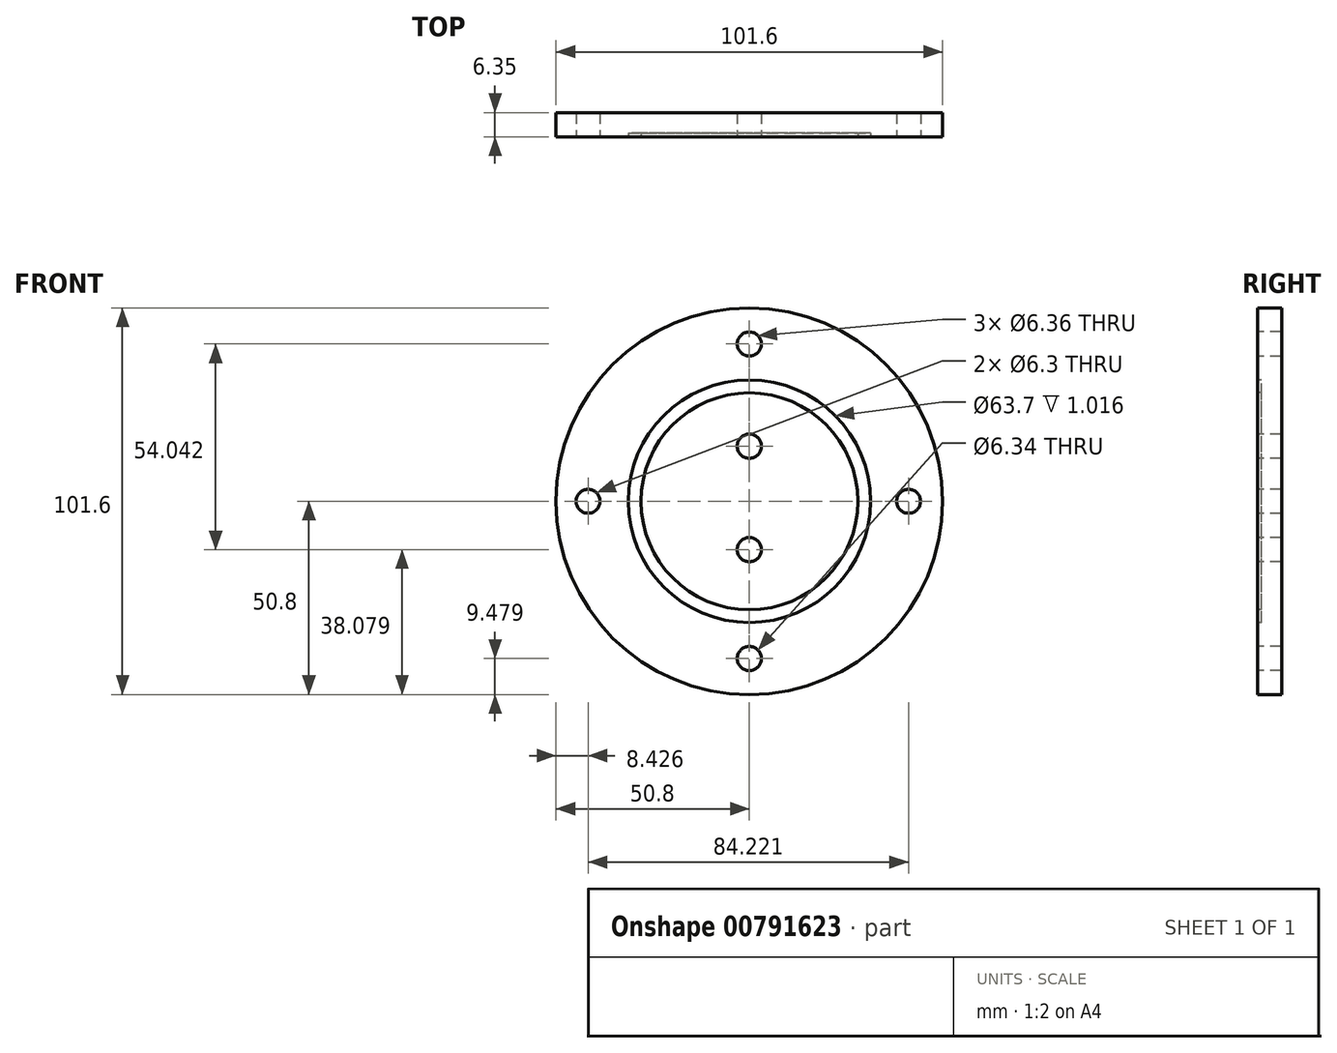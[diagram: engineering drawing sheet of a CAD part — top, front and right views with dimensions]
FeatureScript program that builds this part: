
annotation { "Feature Type Name" : "Feature", "Feature Type Description" : "" }
export const myFeature = defineFeature(function(context is Context, id is Id, definition is map)
    precondition{}
    {
        {
            var Q0;
            Q0=qCreatedBy(makeId("Front.planeOp"),FACE);
            var sketch = newSketch(context, id + "F0", { "sketchPlane" : qUnion([Q0])});
            skCircle(sketch, "E0", {"center": v(0, 0) * mm, "radius": 50.8 * mm});
            skSolve(sketch);
        }
        {
            var Q0;
            Q0 = qSketchRegion(id + "F0", true);
            extrude(context, id + "F1", {"entities" : qUnion([Q0]), "depth" : 6.35 * mm, "offsetDistance" : 25.4 * mm});
        }
        {
            var Q0;
            Q0=makeQuery(id+"F1.opExtrude","CAP_FACE",FACE,{"disambiguationData":[OSD([sQuery(id+"F0.wireOp",EDGE,"E0")])],"isStart":false});
            var sketch = newSketch(context, id + "F2", { "sketchPlane" : qUnion([Q0])});
            skCircle(sketch, "E1", {"center": v(0, 0) * mm, "radius": 28.5 * mm});
            skCircle(sketch, "E2", {"center": v(0, 0) * mm, "radius": 31.85 * mm});
            skSolve(sketch);
        }
        {
            var Q0;
            Q0=makeQuery(id+"F2.imprint","IMPRINT",FACE,{"disambiguationData":[TD([[makeQuery(id+"F2.imprint","IMPRINT",EDGE,{"derivedFrom":sQuery(id+"F2.wireOp",EDGE,"E1")}),-1.0]])]});
            extrude(context, id + "F3", {"entities" : qUnion([Q0]), "operationType" : NewBodyOperationType.REMOVE, "oppositeDirection" : true, "depth" : 1.02 * mm, "offsetDistance" : 25.4 * mm});
        }
        {
            var Q0;
            Q0=makeQuery(id+"F3.boolean.opBoolean","SPLIT",FACE,{"disambiguationData":[TD([makeQuery(id+"F3.opExtrude","SWEPT_FACE",FACE,{"disambiguationData":[OSD([sQuery(id+"F2.wireOp",EDGE,"E1")])]})])],"derivedFrom":makeQuery(id+"F1.opExtrude","CAP_FACE",FACE,{"disambiguationData":[OSD([sQuery(id+"F0.wireOp",EDGE,"E0")])],"isStart":false})});
            var sketch = newSketch(context, id + "F4", { "sketchPlane" : qUnion([Q0])});
            skCircle(sketch, "E3", {"center": v(0, 14.48) * mm, "radius": 3.18 * mm});
            skCircle(sketch, "E4", {"center": v(0, -9.21) * mm, "radius": 3.2 * mm});
            skSolve(sketch);
        }
        {
            var Q0;
            Q0=makeQuery(id+"F4.imprint","IMPRINT",FACE,{"disambiguationData":[TD([[makeQuery(id+"F4.imprint","IMPRINT",EDGE,{"derivedFrom":sQuery(id+"F4.wireOp",EDGE,"E3")}),1.0]])]});
            extrude(context, id + "F5", {"entities" : qUnion([Q0]), "operationType" : NewBodyOperationType.REMOVE, "oppositeDirection" : true, "depth" : 25.4 * mm, "offsetDistance" : 25.4 * mm});
        }
        {
            var Q0;
            Q0=makeQuery(id+"F3.boolean.opBoolean","SPLIT",FACE,{"disambiguationData":[TD([makeQuery(id+"F3.opExtrude","SWEPT_FACE",FACE,{"disambiguationData":[OSD([sQuery(id+"F2.wireOp",EDGE,"E1")])]})])],"derivedFrom":makeQuery(id+"F1.opExtrude","CAP_FACE",FACE,{"disambiguationData":[OSD([sQuery(id+"F0.wireOp",EDGE,"E0")])],"isStart":false})});
            var sketch = newSketch(context, id + "F6", { "sketchPlane" : qUnion([Q0])});
            skCircle(sketch, "E5", {"center": v(0, -12.72) * mm, "radius": 3.18 * mm});
            skSolve(sketch);
        }
        {
            var Q0;
            Q0=makeQuery(id+"F6.imprint","IMPRINT",FACE,{"disambiguationData":[TD([[makeQuery(id+"F6.imprint","IMPRINT",EDGE,{"derivedFrom":sQuery(id+"F6.wireOp",EDGE,"E5")}),1.0]])]});
            extrude(context, id + "F7", {"entities" : qUnion([Q0]), "operationType" : NewBodyOperationType.REMOVE, "oppositeDirection" : true, "depth" : 25.4 * mm, "offsetDistance" : 25.4 * mm});
        }
        {
            var Q0;
            {var subQ0=sQuery(id+"F0.wireOp",EDGE,"E0");Q0=makeQuery(id+"F3.boolean.opBoolean","SPLIT",FACE,{"disambiguationData":[TD([makeQuery(id+"F1.opExtrude","SWEPT_FACE",FACE,{"disambiguationData":[OSD([subQ0])]})])],"derivedFrom":makeQuery(id+"F1.opExtrude","CAP_FACE",FACE,{"disambiguationData":[OSD([subQ0])],"isStart":false})});}
            var sketch = newSketch(context, id + "F8", { "sketchPlane" : qUnion([Q0])});
            skCircle(sketch, "E6", {"center": v(0, 41.32) * mm, "radius": 3.18 * mm});
            skSolve(sketch);
        }
        {
            var Q0;
            Q0 = qSketchRegion(id + "F8", true);
            extrude(context, id + "F9", {"entities" : qUnion([Q0]), "operationType" : NewBodyOperationType.REMOVE, "oppositeDirection" : true, "depth" : 25.4 * mm, "offsetDistance" : 25.4 * mm});
        }
        {
            var Q0;
            {var subQ0=sQuery(id+"F0.wireOp",EDGE,"E0");Q0=makeQuery(id+"F3.boolean.opBoolean","SPLIT",FACE,{"disambiguationData":[TD([makeQuery(id+"F1.opExtrude","SWEPT_FACE",FACE,{"disambiguationData":[OSD([subQ0])]})])],"derivedFrom":makeQuery(id+"F1.opExtrude","CAP_FACE",FACE,{"disambiguationData":[OSD([subQ0])],"isStart":false})});}
            var sketch = newSketch(context, id + "F10", { "sketchPlane" : qUnion([Q0])});
            skCircle(sketch, "E7", {"center": v(41.85, 0) * mm, "radius": 3.15 * mm});
            skSolve(sketch);
        }
        {
            var Q0;
            Q0=makeQuery(id+"F10.imprint","IMPRINT",FACE,{"disambiguationData":[TD([[makeQuery(id+"F10.imprint","IMPRINT",EDGE,{"derivedFrom":sQuery(id+"F10.wireOp",EDGE,"E7")}),1.0]])]});
            extrude(context, id + "F11", {"entities" : qUnion([Q0]), "operationType" : NewBodyOperationType.REMOVE, "oppositeDirection" : true, "depth" : 25.4 * mm, "offsetDistance" : 25.4 * mm});
        }
        {
            var Q0;
            {var subQ0=sQuery(id+"F0.wireOp",EDGE,"E0");Q0=makeQuery(id+"F3.boolean.opBoolean","SPLIT",FACE,{"disambiguationData":[TD([makeQuery(id+"F1.opExtrude","SWEPT_FACE",FACE,{"disambiguationData":[OSD([subQ0])]})])],"derivedFrom":makeQuery(id+"F1.opExtrude","CAP_FACE",FACE,{"disambiguationData":[OSD([subQ0])],"isStart":false})});}
            var sketch = newSketch(context, id + "F12", { "sketchPlane" : qUnion([Q0])});
            skCircle(sketch, "E8", {"center": v(0, -41.32) * mm, "radius": 3.17 * mm});
            skSolve(sketch);
        }
        {
            var Q0;
            Q0=makeQuery(id+"F12.imprint","IMPRINT",FACE,{"disambiguationData":[TD([[makeQuery(id+"F12.imprint","IMPRINT",EDGE,{"derivedFrom":sQuery(id+"F12.wireOp",EDGE,"E8")}),1.0]])]});
            extrude(context, id + "F13", {"entities" : qUnion([Q0]), "operationType" : NewBodyOperationType.REMOVE, "oppositeDirection" : true, "depth" : 25.4 * mm, "offsetDistance" : 25.4 * mm});
        }
        {
            var Q0;
            {var subQ0=sQuery(id+"F0.wireOp",EDGE,"E0");Q0=makeQuery(id+"F3.boolean.opBoolean","SPLIT",FACE,{"disambiguationData":[TD([makeQuery(id+"F1.opExtrude","SWEPT_FACE",FACE,{"disambiguationData":[OSD([subQ0])]})])],"derivedFrom":makeQuery(id+"F1.opExtrude","CAP_FACE",FACE,{"disambiguationData":[OSD([subQ0])],"isStart":false})});}
            var sketch = newSketch(context, id + "F14", { "sketchPlane" : qUnion([Q0])});
            skCircle(sketch, "E9", {"center": v(-42.37, 0) * mm, "radius": 3.15 * mm});
            skSolve(sketch);
        }
        {
            var Q0;
            Q0=makeQuery(id+"F14.imprint","IMPRINT",FACE,{"disambiguationData":[TD([[makeQuery(id+"F14.imprint","IMPRINT",EDGE,{"derivedFrom":sQuery(id+"F14.wireOp",EDGE,"E9")}),1.0]])]});
            extrude(context, id + "F15", {"entities" : qUnion([Q0]), "operationType" : NewBodyOperationType.REMOVE, "oppositeDirection" : true, "depth" : 25.4 * mm, "offsetDistance" : 25.4 * mm});
        }
    });
